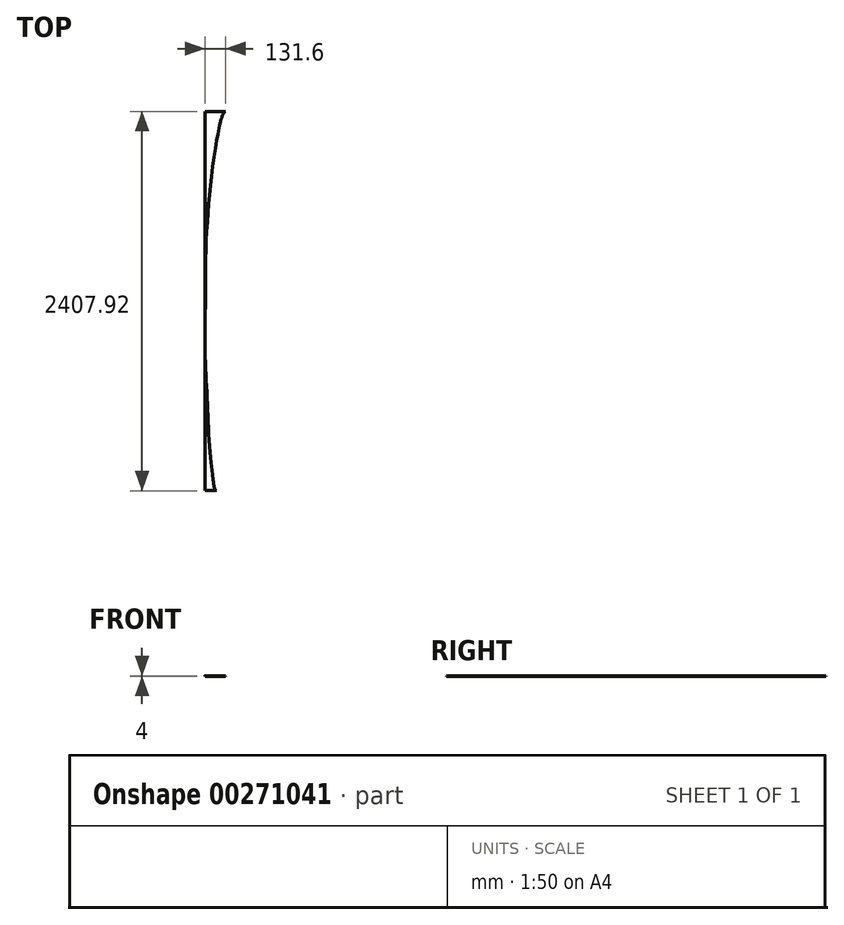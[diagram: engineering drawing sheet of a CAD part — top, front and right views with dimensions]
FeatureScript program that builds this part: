
annotation { "Feature Type Name" : "Feature", "Feature Type Description" : "" }
export const myFeature = defineFeature(function(context is Context, id is Id, definition is map)
    precondition{}
    {
        {
            var Q0;
            Q0=qCreatedBy(makeId("Top.planeOp"),FACE);
            var sketch = newSketch(context, id + "F0", { "sketchPlane" : qUnion([Q0])});
            skFitSpline(sketch, "E0", {"points": [v(25.93, 1100.77) * mm, v(7.3, 1000.77) * mm, v(-22.07, 800.77) * mm, v(-41.27, 600.77) * mm, v(-54.67, 400.77) * mm, v(-60.14, 200.77) * mm, v(-60.8, 0.77) * mm, v(-63.25, -199.23) * mm, v(-60.42, -399.23) * mm, v(-49.6, -599.23) * mm, v(-41.1, -799.23) * mm, v(-27.98, -999.23) * mm, v(-16.44, -1099.23) * mm], "startDerivative": vector(-284.6, -1452.48) * mm, "endDerivative": vector(190.25, -1460.4) * mm});
            skLineSegment(sketch, "E1", {"start": v(10.4, -1203.19) * mm, "end": v(-63.25, -1203.19) * mm});
            skLineSegment(sketch, "E2", {"start": v(68.2, 1204.73) * mm, "end": v(-63.25, 1204.73) * mm});
            skLineSegment(sketch, "E3", {"start": v(-63.25, -1203.19) * mm, "end": v(-63.25, 1204.73) * mm});
            skFitSpline(sketch, "E4", {"points": [v(-16.44, -1099.23) * mm, v(-11.51, -1130.73) * mm, v(-8.93, -1154.14) * mm, v(-4.64, -1179.61) * mm, v(10.4, -1203.19) * mm], "startDerivative": vector(18.95, -121.58) * mm, "endDerivative": vector(97.44, 0) * mm});
            skFitSpline(sketch, "E5", {"points": [v(25.93, 1100.77) * mm, v(36.1, 1144.75) * mm, v(51.92, 1191.83) * mm, v(68.2, 1204.73) * mm], "startDerivative": vector(27.22, 113.33) * mm, "endDerivative": vector(106.14, 0) * mm});
            skSolve(sketch);
        }
        {
            var Q0;
            Q0 = qSketchRegion(id + "F0", true);
            extrude(context, id + "F1", {"entities" : qUnion([Q0]), "depth" : 4 * mm});
        }
    });
